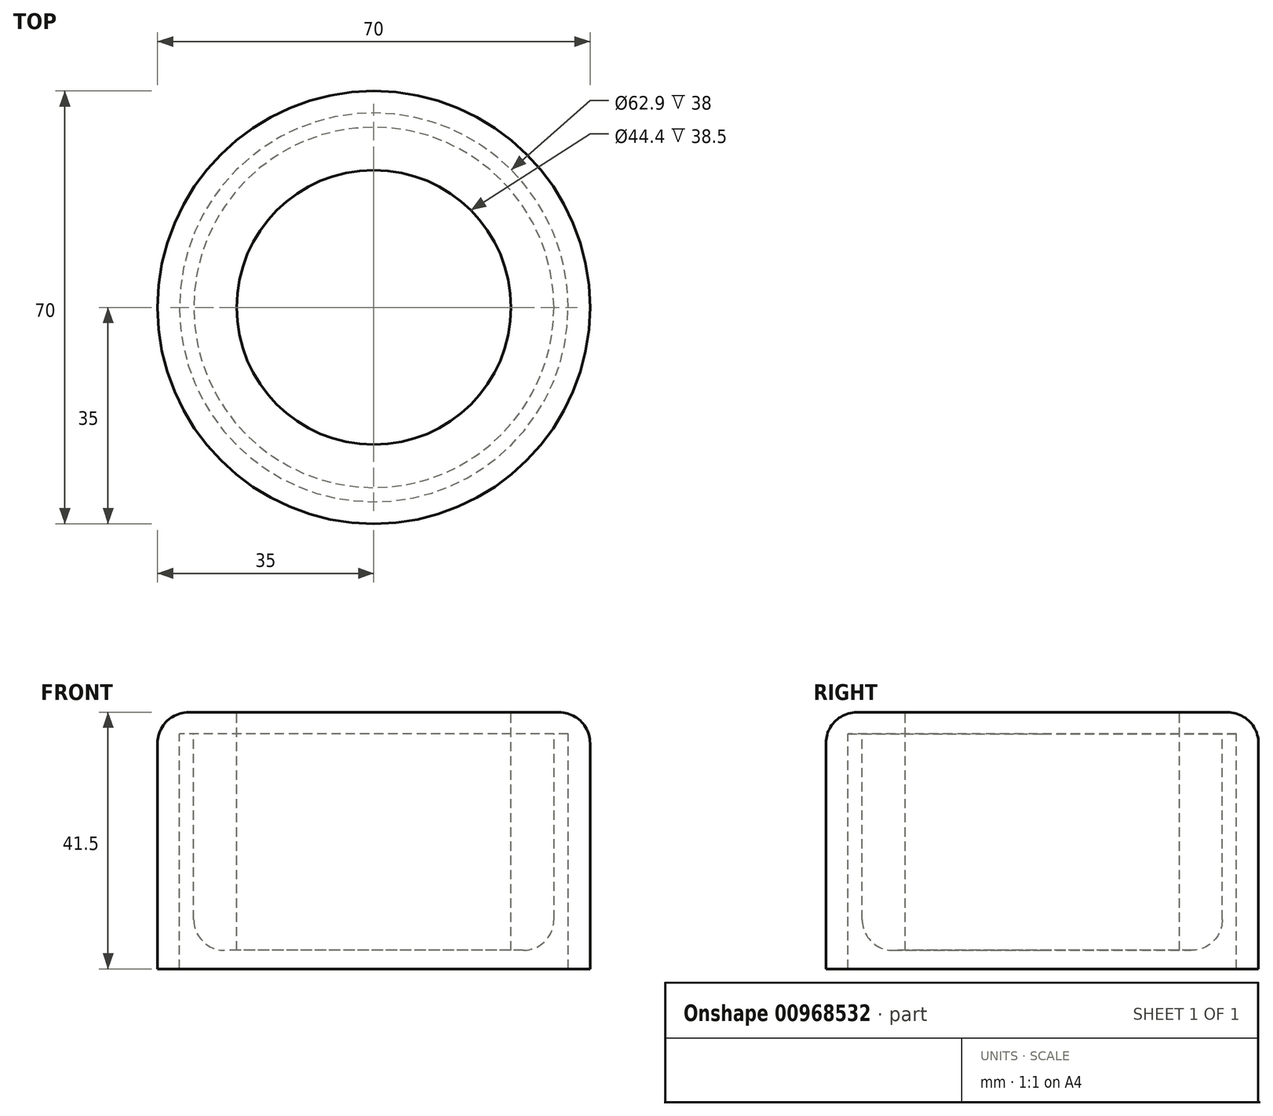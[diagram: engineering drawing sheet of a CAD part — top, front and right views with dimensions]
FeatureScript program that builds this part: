
annotation { "Feature Type Name" : "Feature", "Feature Type Description" : "" }
export const myFeature = defineFeature(function(context is Context, id is Id, definition is map)
    precondition{}
    {
        {
            var Q0;
            Q0=qCreatedBy(makeId("Top.planeOp"),FACE);
            var sketch = newSketch(context, id + "F0", { "sketchPlane" : qUnion([Q0])});
            skCircle(sketch, "E0", {"center": v(0, 0) * mm, "radius": 29.15 * mm});
            skCircle(sketch, "E1", {"center": v(0, 0) * mm, "radius": 31.45 * mm});
            skCircle(sketch, "E2", {"center": v(0, 0) * mm, "radius": 35 * mm});
            skSolve(sketch);
        }
        {
            var Q0;
            Q0 = qSketchRegion(id + "F0", true);
            extrude(context, id + "F1", {"entities" : qUnion([Q0]), "oppositeDirection" : true, "depth" : 38 * mm, "offsetDistance" : 25 * mm});
        }
        {
            var Q0;
            Q0=makeQuery(id+"F0.imprint","IMPRINT",FACE,{"disambiguationData":[TD([[makeQuery(id+"F0.imprint","IMPRINT",EDGE,{"derivedFrom":sQuery(id+"F0.wireOp",EDGE,"E1")}),-1.0]])]});
            var Q1;
            Q1=makeQuery(id+"F0.imprint","IMPRINT",FACE,{"disambiguationData":[TD([[makeQuery(id+"F0.imprint","IMPRINT",EDGE,{"derivedFrom":sQuery(id+"F0.wireOp",EDGE,"E0")}),-1.0]])]});
            var Q2;
            Q2=makeQuery(id+"F0.imprint","IMPRINT",FACE,{"disambiguationData":[TD([[makeQuery(id+"F0.imprint","IMPRINT",EDGE,{"derivedFrom":sQuery(id+"F0.wireOp",EDGE,"E0")}),1.0]])]});
            extrude(context, id + "F2", {"entities" : qUnion([Q0, Q1, Q2]), "operationType" : NewBodyOperationType.ADD, "depth" : 3.5 * mm, "offsetDistance" : 25 * mm});
        }
        {
            var Q0;
            Q0=makeQuery(id+"F2.opExtrude","CAP_FACE",FACE,{"disambiguationData":[OSD([sQuery(id+"F0.wireOp",EDGE,"E2")])],"isStart":false});
            var sketch = newSketch(context, id + "F3", { "sketchPlane" : qUnion([Q0])});
            skCircle(sketch, "E3.0", {"center": v(0, 0) * mm, "radius": 29.15 * mm});
            skCircle(sketch, "E4.0", {"center": v(0, 0) * mm, "radius": 31.45 * mm});
            skCircle(sketch, "E5", {"center": v(0, 0) * mm, "radius": 22.2 * mm});
            skSolve(sketch);
        }
        {
            var Q0;
            Q0=makeQuery(id+"F3.imprint","IMPRINT",FACE,{"disambiguationData":[TD([[makeQuery(id+"F3.imprint","IMPRINT",EDGE,{"derivedFrom":sQuery(id+"F3.wireOp",EDGE,"E5")}),1.0]])]});
            extrude(context, id + "F4", {"entities" : qUnion([Q0]), "operationType" : NewBodyOperationType.REMOVE, "oppositeDirection" : true, "depth" : 25 * mm, "offsetDistance" : 25 * mm});
        }
        {
            var Q0;
            Q0=makeQuery(id+"F0.imprint","IMPRINT",FACE,{"disambiguationData":[TD([[makeQuery(id+"F0.imprint","IMPRINT",EDGE,{"derivedFrom":sQuery(id+"F0.wireOp",EDGE,"E0")}),1.0]])]});
            var sketch = newSketch(context, id + "F5", { "sketchPlane" : qUnion([Q0])});
            skCircle(sketch, "E6", {"center": v(0, 0) * mm, "radius": 25.5 * mm});
            skCircle(sketch, "E7.0", {"center": v(0, 0) * mm, "radius": 22.2 * mm});
            skSolve(sketch);
        }
        {
            var Q0;
            Q0 = qSketchRegion(id + "F5", true);
            extrude(context, id + "F6", {"entities" : qUnion([Q0]), "operationType" : NewBodyOperationType.ADD, "oppositeDirection" : true, "depth" : 35 * mm, "offsetDistance" : 25 * mm});
        }
        {
            var Q0;
            Q0=makeQuery(id+"F0.imprint","IMPRINT",FACE,{"disambiguationData":[TD([[makeQuery(id+"F0.imprint","IMPRINT",EDGE,{"derivedFrom":sQuery(id+"F0.wireOp",EDGE,"E0")}),1.0]])]});
            var sketch = newSketch(context, id + "F7", { "sketchPlane" : qUnion([Q0])});
            skCircle(sketch, "E8.0", {"center": v(0, 0) * mm, "radius": 25.5 * mm});
            skCircle(sketch, "E9.0", {"center": v(0, 0) * mm, "radius": 29.15 * mm});
            skSolve(sketch);
        }
        {
            var Q0;
            Q0 = qSketchRegion(id + "F7", true);
            var Q1;
            Q1=makeQuery(id+"F6.opExtrude","CAP_FACE",FACE,{"disambiguationData":[OSD([sQuery(id+"F5.wireOp",EDGE,"E6"),sQuery(id+"F5.wireOp",EDGE,"E7.0")])],"isStart":false});
            extrude(context, id + "F8", {"entities" : qUnion([Q0]), "operationType" : NewBodyOperationType.ADD, "endBound" : BoundingType.UP_TO_SURFACE, "oppositeDirection" : true, "depth" : 25 * mm, "endBoundEntityFace" : qUnion([Q1]), "offsetDistance" : 25 * mm});
        }
        {
            var Q0;
            Q0=makeQuery(id+"F2.opExtrude","CAP_EDGE",EDGE,{"disambiguationData":[OSD([sQuery(id+"F0.wireOp",EDGE,"E2")])],"isStart":false});
            fillet(context, id + "F9", {"entities" : qUnion([Q0]), "tangentPropagation" : true, "radius" : 5 * mm, "defaultsChanged" : false, "vertexSettings" : [], "allowEdgeOverflow" : false});
        }
        {
            var Q0;
            Q0=makeQuery(id+"F8.opExtrude","CAP_EDGE",EDGE,{"disambiguationData":[OSD([sQuery(id+"F7.wireOp",EDGE,"E9.0")])],"isStart":false});
            fillet(context, id + "F10", {"entities" : qUnion([Q0]), "tangentPropagation" : true, "radius" : 5 * mm, "defaultsChanged" : false, "vertexSettings" : [], "allowEdgeOverflow" : false});
        }
    });
